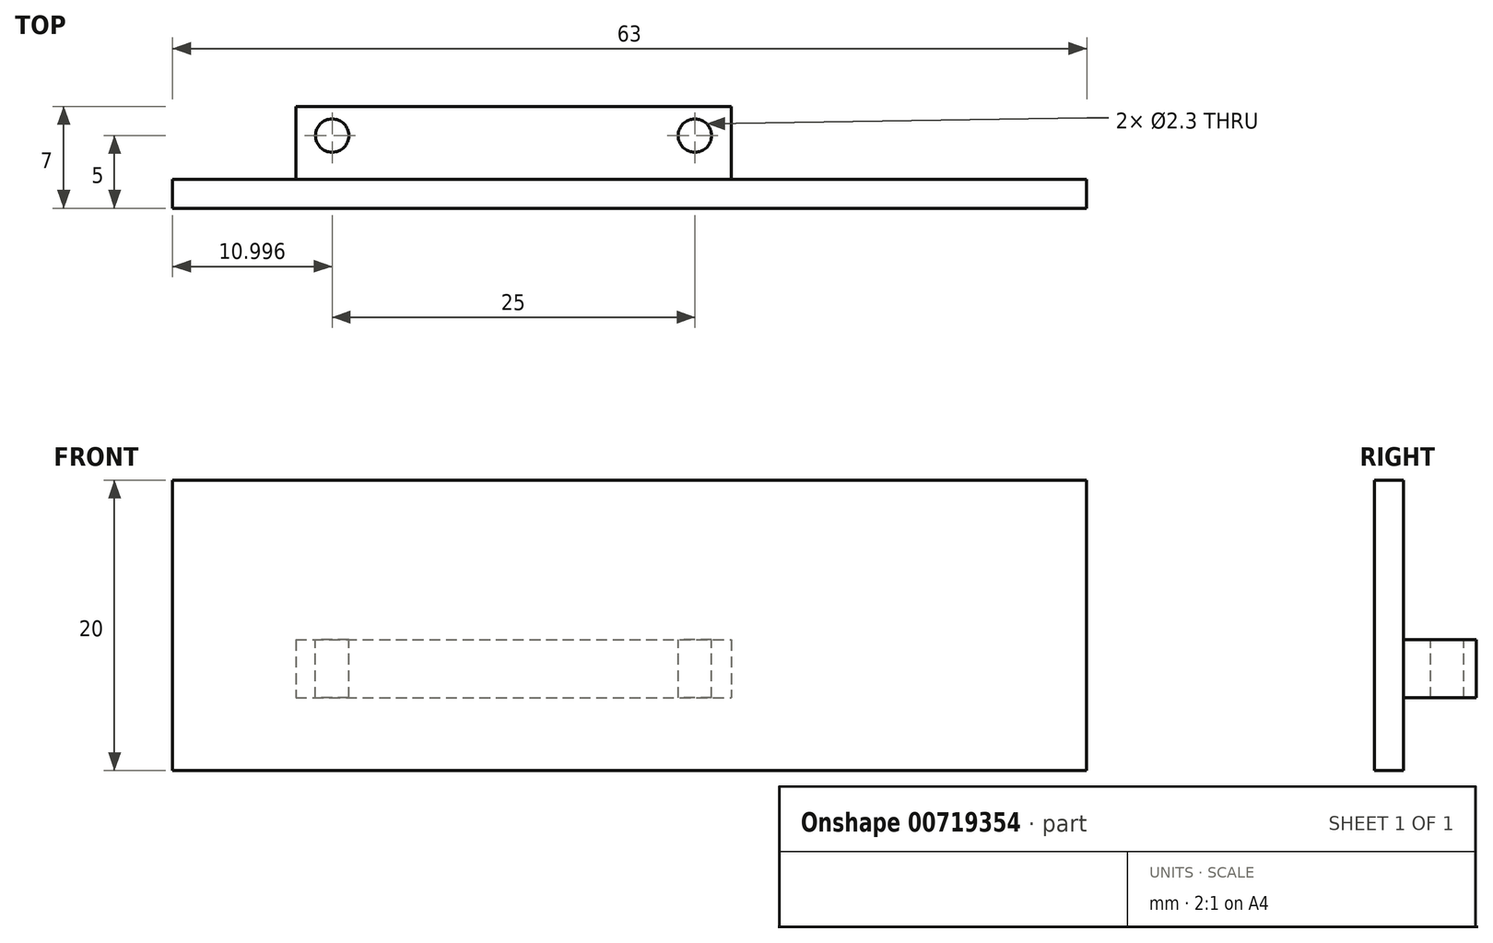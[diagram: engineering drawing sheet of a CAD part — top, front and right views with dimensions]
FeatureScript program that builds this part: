
annotation { "Feature Type Name" : "Feature", "Feature Type Description" : "" }
export const myFeature = defineFeature(function(context is Context, id is Id, definition is map)
    precondition{}
    {
        {
            var Q0;
            Q0=qCreatedBy(makeId("Front.planeOp"),FACE);
            var sketch = newSketch(context, id + "F0", { "sketchPlane" : qUnion([Q0])});
            skLineSegment(sketch, "E0", {"start": v(-32.25, -22.74) * mm, "end": v(-32.25, -32.74) * mm});
            skLineSegment(sketch, "E1", {"start": v(-32.25, -32.74) * mm, "end": v(30.75, -32.74) * mm});
            skLineSegment(sketch, "E2", {"start": v(30.75, -32.74) * mm, "end": v(30.75, -12.74) * mm});
            skLineSegment(sketch, "E3", {"start": v(30.75, -12.74) * mm, "end": v(-32.25, -12.74) * mm});
            skLineSegment(sketch, "E4", {"start": v(-32.25, -12.74) * mm, "end": v(-32.25, -22.74) * mm});
            skSolve(sketch);
        }
        {
            var Q0;
            Q0=qSketchRegion(id+"F0",true);
            extrude(context, id + "F1", {"entities" : qUnion([Q0]), "depth" : 2 * mm, "offsetDistance" : 25 * mm});
        }
        {
            var Q0;
            Q0=makeQuery(id+"F1.opExtrude","CAP_FACE",FACE,{"disambiguationData":[OSD([sQuery(id+"F0.wireOp",EDGE,"E0"),sQuery(id+"F0.wireOp",EDGE,"E1"),sQuery(id+"F0.wireOp",EDGE,"E2"),sQuery(id+"F0.wireOp",EDGE,"E3"),sQuery(id+"F0.wireOp",EDGE,"E4")])],"isStart":false});
            var sketch = newSketch(context, id + "F2", { "sketchPlane" : qUnion([Q0])});
            skLineSegment(sketch, "E5.bottom", {"start": v(-23.75, -23.74) * mm, "end": v(6.25, -23.74) * mm});
            skLineSegment(sketch, "E5.top", {"start": v(-23.75, -27.74) * mm, "end": v(6.25, -27.74) * mm});
            skLineSegment(sketch, "E5.left", {"start": v(-23.75, -23.74) * mm, "end": v(-23.75, -27.74) * mm});
            skLineSegment(sketch, "E5.right", {"start": v(6.25, -23.74) * mm, "end": v(6.25, -27.74) * mm});
            skSolve(sketch);
        }
        {
            var Q0;
            Q0=qSketchRegion(id+"F2",true);
            extrude(context, id + "F3", {"entities" : qUnion([Q0]), "operationType" : NewBodyOperationType.ADD, "depth" : 5 * mm, "offsetDistance" : 25 * mm});
        }
        {
            var Q0;
            Q0=makeQuery(id+"F3.opExtrude","SWEPT_FACE",FACE,{"disambiguationData":[OSD([sQuery(id+"F2.wireOp",EDGE,"E5.bottom")])]});
            var sketch = newSketch(context, id + "F4", { "sketchPlane" : qUnion([Q0])});
            skCircle(sketch, "E6", {"center": v(-21.25, -5) * mm, "radius": 1.15 * mm});
            skCircle(sketch, "E7", {"center": v(3.75, -5) * mm, "radius": 1.15 * mm});
            skSolve(sketch);
        }
        {
            var Q0;
            Q0=qSketchRegion(id+"F4",true);
            extrude(context, id + "F5", {"entities" : qUnion([Q0]), "operationType" : NewBodyOperationType.REMOVE, "oppositeDirection" : true, "depth" : 25 * mm, "offsetDistance" : 25 * mm});
        }
        {
            var Q0;
            Q0=makeQuery(id+"F1.opExtrude","SWEPT_BODY",BODY,{"disambiguationData":[OSD([sQuery(id+"F0.wireOp",EDGE,"E0"),sQuery(id+"F0.wireOp",EDGE,"E1"),sQuery(id+"F0.wireOp",EDGE,"E2"),sQuery(id+"F0.wireOp",EDGE,"E3"),sQuery(id+"F0.wireOp",EDGE,"E4")])]});
            var Q1;
            Q1=qCreatedBy(makeId("Front.planeOp"),FACE);
            mirror(context, id + "F6", {"entities" : qUnion([Q0]), "mirrorPlane" : qUnion([Q1])});
        }
        {
            var Q0;
            Q0=makeQuery(id+"F1.opExtrude","SWEPT_BODY",BODY,{"disambiguationData":[OSD([sQuery(id+"F0.wireOp",EDGE,"E0"),sQuery(id+"F0.wireOp",EDGE,"E1"),sQuery(id+"F0.wireOp",EDGE,"E2"),sQuery(id+"F0.wireOp",EDGE,"E3"),sQuery(id+"F0.wireOp",EDGE,"E4")])]});
            deleteBodies(context, id + "F7", {"entities" : qUnion([Q0])});
        }
    });
